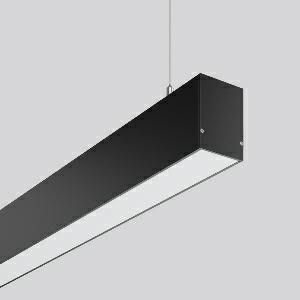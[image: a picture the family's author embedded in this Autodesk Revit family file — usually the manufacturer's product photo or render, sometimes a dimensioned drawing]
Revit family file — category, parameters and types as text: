
# Revit family: less_is_more_50_312312_003_1_76_aec0
name_source: partatom
category: Lighting Fixtures
units: mm (PartAtom-declared; Revit-internal decimal feet)

## family parameters
Cut with Voids When Loaded = No
Host = Face
Light Source = No
Part Type = Normal
Room Calculation Point = No
Round Connector Dimension = Use Diameter
Shared = No

## types (1)
- LESS IS MORE 50 (1 x LED Modul 840, 3250 lm, 4000)
    Apparent Load = 28 VA
    CIE Flux Codes = 48 79 95 100 100
    Color Rendering = 80
    Color Temperature = 4000
    Default Elevation = 1800 mm
    Description = Series: LESS IS MORE 50
Linear pendant luminaire for aesthetically sophisticated lighting. Housing: extruded aluminium profile, powder-coated. End cap aluminium powder-coated. Canopy made of aluminium, powder-coated. Diffuser made of non-yellowing plastic (PMMA), opal. Direct light emission. Suitable for pendant. 2-point steel cable suspension freely positionable and infinitely height-adjustable. Special lengths available on request. LED unit with integrated converter interchangeable and removable. Suitable for through-wiring. With sensors or as a safety luminaire on request. 
Colour: deep black, matt (RAL 9005)
Length: 1127 mm
Width: 57 mm
Height: 75 mm
Suspension length: 2000 mm
Lamp: LED
Socket: without socket
Colour temperature: 4000K
Colour rendering index (CRI): 80
System power: 28 W
Rated luminous flux: 3250 lm
Luminous efficiency: 116 lm/W
Control gear: Converter, dimmable, DALI
Protection class: I
Type of protection: IP 20
    Height = 75 mm
    Lamp = 1 x LED Modul 840
    Lamp Light Flux = 3250 lm
    Lamp count = 1
    Length = 1127 mm
    Lifetime = 50000 h
    Luminous efficacy = 116 lm/W
    Manufacturer = RZB
    ModVariant = No
    Model = 312312.003.1.76
    Mounting Place = Ceiling
    Mounting Type = Pendant
    Number of Poles = 1
    OnlyDefault = Yes
    Power Factor = 1
    Product Name = LESS IS MORE 50
    Product group = Pendant LED linear luminaires
    ProductGroupID = 907
    Protection Class = Protection class I
    Protection Degree = IP 20
    RLX_Detail_Level = 1
    RLX_Emergency_Light_Flux = 0 lm
    RLX_Emergency_Type = 0
    RLX_Emergency_Type_DB = No
    RlxData = <blob elided: 28921 chars, md5=756df745>
    Socket = socket
    Standby Power = 0 W
    System Light Flux = 3250 lm
    System Power = 28 W
    Type Comments = Product without accessories
    Type Image = 312318.003.jpg
    URL = http://relux.com
    VarID = ---
    Voltage = 230 V
    Voltage Range = 220-240 V
    Weight = 0.00 kg
    Width = 57 mm

## geometry (parser evidence)
native form markers: Blend x4, Sweep x9
no freeform markers — native parametric forms only
